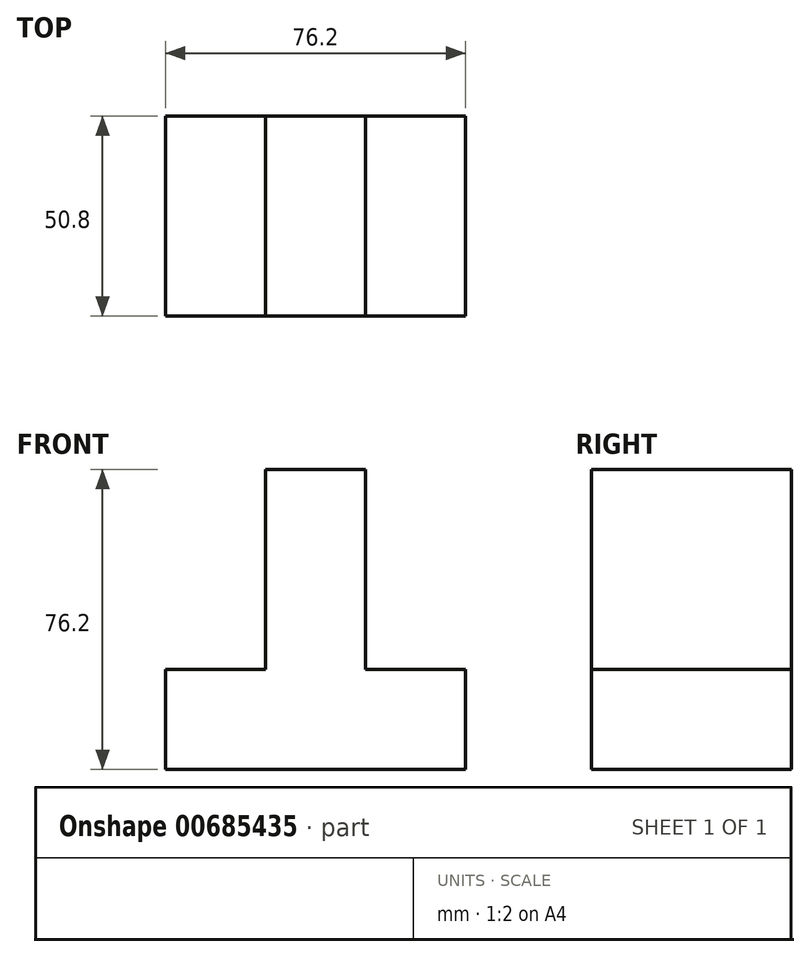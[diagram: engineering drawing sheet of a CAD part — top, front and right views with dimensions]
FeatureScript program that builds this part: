
annotation { "Feature Type Name" : "Feature", "Feature Type Description" : "" }
export const myFeature = defineFeature(function(context is Context, id is Id, definition is map)
    precondition{}
    {
        {
            var Q0;
            Q0=qCreatedBy(makeId("Front.planeOp"),FACE);
            var sketch = newSketch(context, id + "F0", { "sketchPlane" : qUnion([Q0])});
            skLineSegment(sketch, "E0", {"start": v(-8.78, 34.9) * mm, "end": v(-8.78, -15.9) * mm});
            skLineSegment(sketch, "E1", {"start": v(-8.78, -15.9) * mm, "end": v(-34.18, -15.9) * mm});
            skLineSegment(sketch, "E2", {"start": v(-34.18, -15.9) * mm, "end": v(-34.18, -41.3) * mm});
            skLineSegment(sketch, "E3", {"start": v(-8.78, 34.9) * mm, "end": v(16.62, 34.9) * mm});
            skLineSegment(sketch, "E4", {"start": v(16.62, 34.9) * mm, "end": v(16.62, -15.9) * mm});
            skLineSegment(sketch, "E5", {"start": v(16.62, -15.9) * mm, "end": v(42.02, -15.9) * mm});
            skLineSegment(sketch, "E6", {"start": v(42.02, -15.9) * mm, "end": v(42.02, -41.3) * mm});
            skLineSegment(sketch, "E7", {"start": v(-34.18, -41.3) * mm, "end": v(42.02, -41.3) * mm});
            skSolve(sketch);
        }
        {
            var Q0;
            Q0 = qSketchRegion(id + "F0", true);
            extrude(context, id + "F1", {"entities" : qUnion([Q0]), "depth" : 50.8 * mm, "offsetDistance" : 25.4 * mm});
        }
    });
